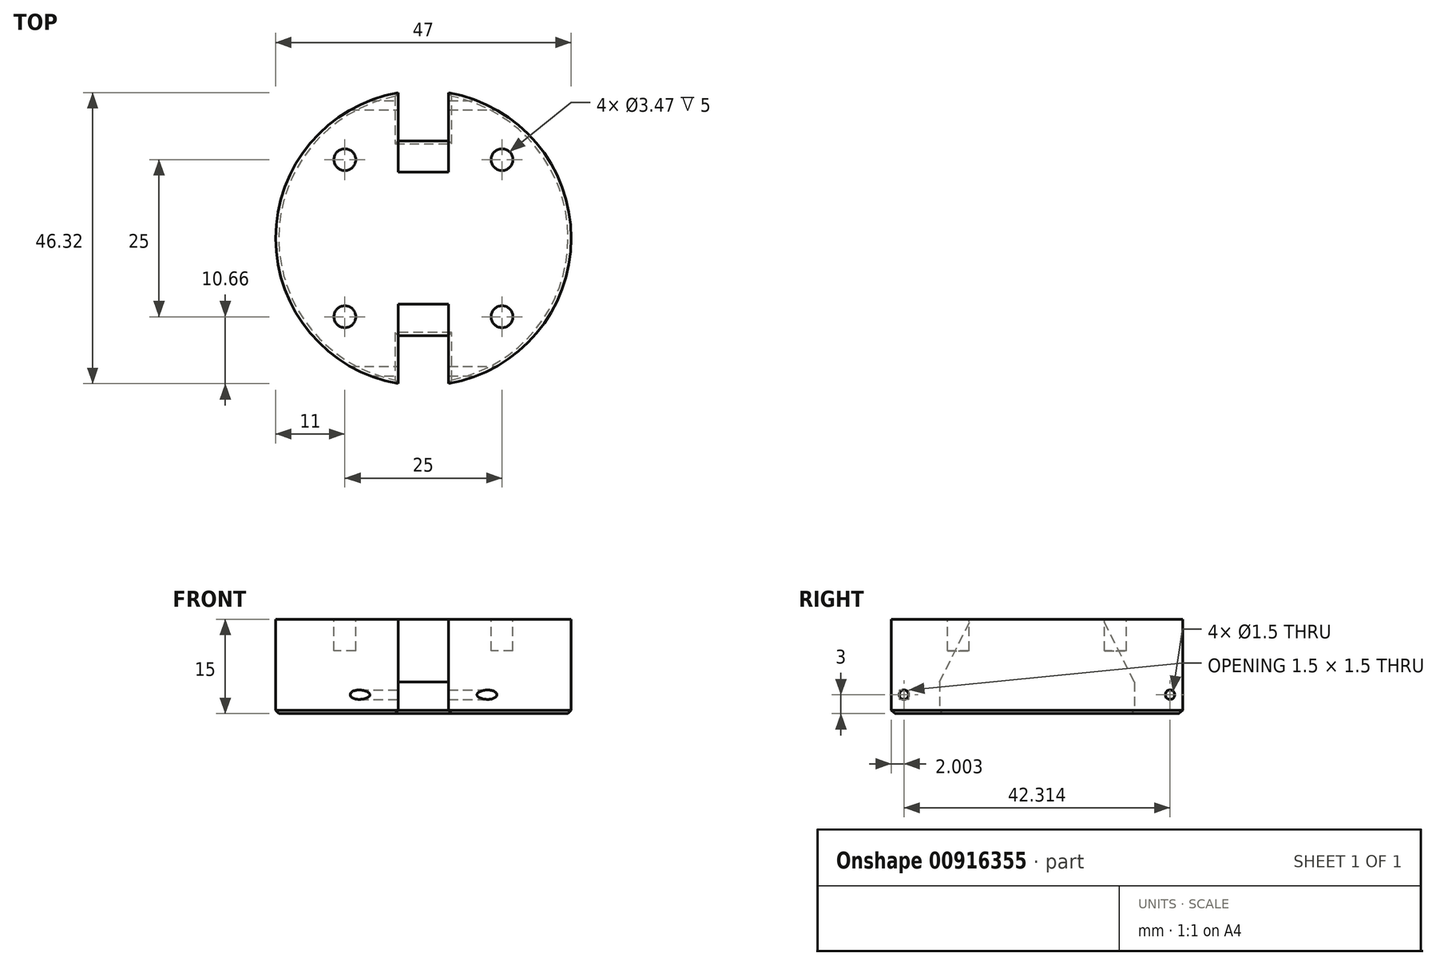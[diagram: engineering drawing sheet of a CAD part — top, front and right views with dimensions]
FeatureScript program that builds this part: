
annotation { "Feature Type Name" : "Feature", "Feature Type Description" : "" }
export const myFeature = defineFeature(function(context is Context, id is Id, definition is map)
    precondition{}
    {
        {
            var Q0;
            Q0=qCreatedBy(makeId("Top.planeOp"),FACE);
            var sketch = newSketch(context, id + "F0", { "sketchPlane" : qUnion([Q0])});
            skCircle(sketch, "E0", {"center": v(0, 0) * mm, "radius": 23.5 * mm});
            skSolve(sketch);
        }
        {
            var Q0;
            Q0=makeQuery(id+"F0.imprint","IMPRINT",FACE,{"disambiguationData":[TD([[makeQuery(id+"F0.imprint","IMPRINT",EDGE,{"derivedFrom":sQuery(id+"F0.wireOp",EDGE,"E0")}),1.0]])]});
            extrude(context, id + "F1", {"entities" : qUnion([Q0]), "depth" : 15 * mm, "offsetDistance" : 25 * mm});
        }
        {
            var Q0;
            Q0=makeQuery(id+"F1.opExtrude","CAP_FACE",FACE,{"disambiguationData":[OSD([sQuery(id+"F0.wireOp",EDGE,"E0")])],"isStart":true});
            var sketch = newSketch(context, id + "F2", { "sketchPlane" : qUnion([Q0])});
            skLineSegment(sketch, "E1.bottom", {"start": v(0, 23.5) * mm, "end": v(4, 23.5) * mm});
            skLineSegment(sketch, "E1.top", {"start": v(0, 15.5) * mm, "end": v(4, 15.5) * mm});
            skLineSegment(sketch, "E1.left", {"start": v(0, 23.5) * mm, "end": v(0, 15.5) * mm});
            skLineSegment(sketch, "E1.right", {"start": v(4, 23.5) * mm, "end": v(4, 15.5) * mm});
            skLineSegment(sketch, "E2.MirrorCS", {"start": v(0, 23.5) * mm, "end": v(-4, 23.5) * mm});
            skLineSegment(sketch, "E3.MirrorCS", {"start": v(0, 15.5) * mm, "end": v(-4, 15.5) * mm});
            skLineSegment(sketch, "E4.MirrorCS", {"start": v(-4, 23.5) * mm, "end": v(-4, 15.5) * mm});
            skLineSegment(sketch, "E5.MirrorCS", {"start": v(0, -23.5) * mm, "end": v(0, -15.5) * mm});
            skLineSegment(sketch, "E6.MirrorCS", {"start": v(0, -15.5) * mm, "end": v(-4, -15.5) * mm});
            skLineSegment(sketch, "E7.MirrorCS", {"start": v(4, -23.5) * mm, "end": v(4, -15.5) * mm});
            skLineSegment(sketch, "E8.MirrorCS", {"start": v(0, -15.5) * mm, "end": v(4, -15.5) * mm});
            skLineSegment(sketch, "E9.MirrorCS", {"start": v(0, -23.5) * mm, "end": v(-4, -23.5) * mm});
            skLineSegment(sketch, "E10.MirrorCS", {"start": v(0, -23.5) * mm, "end": v(4, -23.5) * mm});
            skLineSegment(sketch, "E11.MirrorCS", {"start": v(-4, -23.5) * mm, "end": v(-4, -15.5) * mm});
            skSolve(sketch);
        }
        {
            var Q0;
            {var subQ0=sQuery(id+"F2.wireOp",EDGE,"E9.MirrorCS");Q0=makeQuery(id+"F2.imprint","IMPRINT",FACE,{"disambiguationData":[TD([[makeQuery(id+"F2.imprint","IMPRINT",EDGE,{"derivedFrom":subQ0}),-1.0]])]});}
            var Q1;
            {var subQ0=sQuery(id+"F2.wireOp",EDGE,"E10.MirrorCS");Q1=makeQuery(id+"F2.imprint","IMPRINT",FACE,{"disambiguationData":[TD([[makeQuery(id+"F2.imprint","IMPRINT",EDGE,{"derivedFrom":subQ0}),1.0]])]});}
            var Q2;
            {var subQ0=sQuery(id+"F2.wireOp",EDGE,"E6.MirrorCS");Q2=makeQuery(id+"F2.imprint","IMPRINT",FACE,{"disambiguationData":[TD([[makeQuery(id+"F2.imprint","IMPRINT",EDGE,{"derivedFrom":subQ0}),1.0]])]});}
            var Q3;
            {var subQ4=sQuery(id+"F2.wireOp",EDGE,"E5.MirrorCS");Q3=makeQuery(id+"F2.imprint","IMPRINT",FACE,{"disambiguationData":[TD([[makeQuery(id+"F2.imprint","IMPRINT",EDGE,{"derivedFrom":subQ4}),-1.0]])]});}
            var Q4;
            {var subQ0=sQuery(id+"F2.wireOp",EDGE,"E1.top");Q4=makeQuery(id+"F2.imprint","IMPRINT",FACE,{"disambiguationData":[TD([[makeQuery(id+"F2.imprint","IMPRINT",EDGE,{"derivedFrom":subQ0}),1.0]])]});}
            var Q5;
            {var subQ0=sQuery(id+"F2.wireOp",EDGE,"E1.left");Q5=makeQuery(id+"F2.imprint","IMPRINT",FACE,{"disambiguationData":[TD([[makeQuery(id+"F2.imprint","IMPRINT",EDGE,{"derivedFrom":subQ0}),-1.0]])]});}
            var Q6;
            {var subQ0=sQuery(id+"F2.wireOp",EDGE,"E1.bottom");Q6=makeQuery(id+"F2.imprint","IMPRINT",FACE,{"disambiguationData":[TD([[makeQuery(id+"F2.imprint","IMPRINT",EDGE,{"derivedFrom":subQ0}),-1.0]])]});}
            var Q7;
            {var subQ0=sQuery(id+"F2.wireOp",EDGE,"E2.MirrorCS");Q7=makeQuery(id+"F2.imprint","IMPRINT",FACE,{"disambiguationData":[TD([[makeQuery(id+"F2.imprint","IMPRINT",EDGE,{"derivedFrom":subQ0}),1.0]])]});}
            extrude(context, id + "F3", {"entities" : qUnion([Q0, Q1, Q2, Q3, Q4, Q5, Q6, Q7]), "operationType" : NewBodyOperationType.REMOVE, "oppositeDirection" : true, "depth" : 25 * mm, "offsetDistance" : 25 * mm});
        }
        {
            var Q0;
            Q0=makeQuery(id+"F3.boolean.opBoolean","INTERSECT",EDGE,{"derivedFrom":[makeQuery(id+"F1.opExtrude","CAP_FACE",FACE,{"disambiguationData":[OSD([sQuery(id+"F0.wireOp",EDGE,"E0")])],"isStart":false}),makeQuery(id+"F3.opExtrude","SWEPT_FACE",FACE,{"disambiguationData":[OSD([sQuery(id+"F2.wireOp",EDGE,"E1.top"),sQuery(id+"F2.wireOp",EDGE,"E3.MirrorCS")])]})]});
            chamfer(context, id + "F4", {"entities" : qUnion([Q0]), "chamferType" : ChamferType.TWO_OFFSETS, "width1" : 10 * mm, "oppositeDirection" : false, "width2" : 5 * mm, "tangentPropagation" : true});
        }
        {
            var Q0;
            Q0=makeQuery(id+"F3.boolean.opBoolean","INTERSECT",EDGE,{"derivedFrom":[makeQuery(id+"F1.opExtrude","CAP_FACE",FACE,{"disambiguationData":[OSD([sQuery(id+"F0.wireOp",EDGE,"E0")])],"isStart":false}),makeQuery(id+"F3.opExtrude","SWEPT_FACE",FACE,{"disambiguationData":[OSD([sQuery(id+"F2.wireOp",EDGE,"E6.MirrorCS"),sQuery(id+"F2.wireOp",EDGE,"E8.MirrorCS")])]})]});
            chamfer(context, id + "F5", {"entities" : qUnion([Q0]), "chamferType" : ChamferType.TWO_OFFSETS, "width1" : 10 * mm, "oppositeDirection" : false, "width2" : 5 * mm, "tangentPropagation" : true});
        }
        {
            var Q0;
            Q0=qCreatedBy(makeId("Right.planeOp"),FACE);
            var sketch = newSketch(context, id + "F6", { "sketchPlane" : qUnion([Q0])});
            skLineSegment(sketch, "E12.bottom", {"start": v(-23.16, 0) * mm, "end": v(-21.16, 0) * mm});
            skLineSegment(sketch, "E12.top", {"start": v(-23.16, 3) * mm, "end": v(-21.16, 3) * mm});
            skLineSegment(sketch, "E12.left", {"start": v(-23.16, 0) * mm, "end": v(-23.16, 3) * mm});
            skLineSegment(sketch, "E12.right", {"start": v(-21.16, 0) * mm, "end": v(-21.16, 3) * mm});
            skCircle(sketch, "E13", {"center": v(-21.16, 3) * mm, "radius": 0.75 * mm});
            skSolve(sketch);
        }
        {
            var Q0;
            Q0=qCreatedBy(makeId("Right.planeOp"),FACE);
            var sketch = newSketch(context, id + "F7", { "sketchPlane" : qUnion([Q0])});
            skCircle(sketch, "E14", {"center": v(-21.16, 3) * mm, "radius": 0.75 * mm});
            skCircle(sketch, "E15.MirrorC", {"center": v(21.16, 3) * mm, "radius": 0.75 * mm});
            skSolve(sketch);
        }
        {
            var Q0;
            Q0 = qSketchRegion(id + "F7", true);
            extrude(context, id + "F8", {"entities" : qUnion([Q0]), "operationType" : NewBodyOperationType.REMOVE, "endBound" : BoundingType.SYMMETRIC, "oppositeDirection" : true, "depth" : 25 * mm, "offsetDistance" : 25 * mm});
        }
        {
            var Q0;
            Q0=makeQuery(id+"F1.opExtrude","CAP_FACE",FACE,{"disambiguationData":[OSD([sQuery(id+"F0.wireOp",EDGE,"E0")])],"isStart":false});
            var sketch = newSketch(context, id + "F9", { "sketchPlane" : qUnion([Q0])});
            skLineSegment(sketch, "E16.bottom", {"start": v(12.5, 12.5) * mm, "end": v(-12.5, 12.5) * mm});
            skLineSegment(sketch, "E16.top", {"start": v(12.5, -12.5) * mm, "end": v(-12.5, -12.5) * mm});
            skLineSegment(sketch, "E16.left", {"start": v(12.5, 12.5) * mm, "end": v(12.5, -12.5) * mm});
            skLineSegment(sketch, "E16.right", {"start": v(-12.5, 12.5) * mm, "end": v(-12.5, -12.5) * mm});
            skPoint(sketch, "E16.middle", {"position": v(0, 0) * mm});
            skSolve(sketch);
        }
        {
            var Q0;
            {var subQ7=sQuery(id+"F9.wireOp",EDGE,"E16.left");Q0=makeQuery(id+"F9.imprint","IMPRINT",FACE,{"disambiguationData":[TD([[makeQuery(id+"F9.imprint","IMPRINT",EDGE,{"derivedFrom":subQ7}),-1.0]])]});}
            var sketch = newSketch(context, id + "F10", { "sketchPlane" : qUnion([Q0])});
            skCircle(sketch, "E17", {"center": v(-12.5, 12.5) * mm, "radius": 1.74 * mm});
            skCircle(sketch, "E18", {"center": v(12.5, -12.5) * mm, "radius": 1.74 * mm});
            skCircle(sketch, "E19", {"center": v(12.5, 12.5) * mm, "radius": 1.74 * mm});
            skCircle(sketch, "E20", {"center": v(-12.5, -12.5) * mm, "radius": 1.74 * mm});
            skSolve(sketch);
        }
        {
            var Q0;
            {var subQ0=sQuery(id+"F10.wireOp",EDGE,"E17");var subQ1=sQuery(id+"F9.wireOp",EDGE,"E16.right");var subQ5=makeQuery(id+"F9.imprint","IMPRINT",EDGE,{"derivedFrom":subQ1});var subQ6=makeQuery(id+"F10.imprint","INTERSECT",VERTEX,{"derivedFrom":[subQ5,subQ0]});Q0=makeQuery(id+"F10.imprint","IMPRINT",FACE,{"disambiguationData":[TD([[makeQuery(id+"F10.imprint","IMPRINT",EDGE,{"disambiguationData":[TD([[subQ6,1.0]])],"derivedFrom":subQ0}),1.0]])]});}
            var Q1;
            {var subQ0=sQuery(id+"F10.wireOp",EDGE,"E17");var subQ1=sQuery(id+"F9.wireOp",EDGE,"E16.right");var subQ5=makeQuery(id+"F9.imprint","IMPRINT",EDGE,{"derivedFrom":subQ1});var subQ6=makeQuery(id+"F10.imprint","INTERSECT",VERTEX,{"derivedFrom":[subQ5,subQ0]});Q1=makeQuery(id+"F10.imprint","IMPRINT",FACE,{"disambiguationData":[TD([[makeQuery(id+"F10.imprint","IMPRINT",EDGE,{"disambiguationData":[TD([[subQ6,-1.0]])],"derivedFrom":subQ0}),1.0]])]});}
            var Q2;
            {var subQ0=sQuery(id+"F10.wireOp",EDGE,"E20");var subQ1=sQuery(id+"F9.wireOp",EDGE,"E16.right");var subQ5=makeQuery(id+"F9.imprint","IMPRINT",EDGE,{"derivedFrom":subQ1});var subQ6=makeQuery(id+"F10.imprint","INTERSECT",VERTEX,{"derivedFrom":[subQ5,subQ0]});Q2=makeQuery(id+"F10.imprint","IMPRINT",FACE,{"disambiguationData":[TD([[makeQuery(id+"F10.imprint","IMPRINT",EDGE,{"disambiguationData":[TD([[subQ6,-1.0]])],"derivedFrom":subQ0}),1.0]])]});}
            var Q3;
            {var subQ0=sQuery(id+"F10.wireOp",EDGE,"E20");var subQ1=sQuery(id+"F9.wireOp",EDGE,"E16.right");var subQ5=makeQuery(id+"F9.imprint","IMPRINT",EDGE,{"derivedFrom":subQ1});var subQ6=makeQuery(id+"F10.imprint","INTERSECT",VERTEX,{"derivedFrom":[subQ5,subQ0]});Q3=makeQuery(id+"F10.imprint","IMPRINT",FACE,{"disambiguationData":[TD([[makeQuery(id+"F10.imprint","IMPRINT",EDGE,{"disambiguationData":[TD([[subQ6,1.0]])],"derivedFrom":subQ0}),1.0]])]});}
            var Q4;
            {var subQ0=sQuery(id+"F10.wireOp",EDGE,"E18");var subQ1=sQuery(id+"F9.wireOp",EDGE,"E16.left");var subQ5=makeQuery(id+"F9.imprint","IMPRINT",EDGE,{"derivedFrom":subQ1});var subQ6=makeQuery(id+"F10.imprint","INTERSECT",VERTEX,{"derivedFrom":[subQ5,subQ0]});Q4=makeQuery(id+"F10.imprint","IMPRINT",FACE,{"disambiguationData":[TD([[makeQuery(id+"F10.imprint","IMPRINT",EDGE,{"disambiguationData":[TD([[subQ6,1.0]])],"derivedFrom":subQ0}),1.0]])]});}
            var Q5;
            {var subQ0=sQuery(id+"F10.wireOp",EDGE,"E19");var subQ1=sQuery(id+"F9.wireOp",EDGE,"E16.left");var subQ5=makeQuery(id+"F9.imprint","IMPRINT",EDGE,{"derivedFrom":subQ1});var subQ6=makeQuery(id+"F10.imprint","INTERSECT",VERTEX,{"derivedFrom":[subQ5,subQ0]});Q5=makeQuery(id+"F10.imprint","IMPRINT",FACE,{"disambiguationData":[TD([[makeQuery(id+"F10.imprint","IMPRINT",EDGE,{"disambiguationData":[TD([[subQ6,-1.0]])],"derivedFrom":subQ0}),1.0]])]});}
            var Q6;
            {var subQ0=sQuery(id+"F10.wireOp",EDGE,"E19");var subQ1=sQuery(id+"F9.wireOp",EDGE,"E16.left");var subQ5=makeQuery(id+"F9.imprint","IMPRINT",EDGE,{"derivedFrom":subQ1});var subQ6=makeQuery(id+"F10.imprint","INTERSECT",VERTEX,{"derivedFrom":[subQ5,subQ0]});Q6=makeQuery(id+"F10.imprint","IMPRINT",FACE,{"disambiguationData":[TD([[makeQuery(id+"F10.imprint","IMPRINT",EDGE,{"disambiguationData":[TD([[subQ6,1.0]])],"derivedFrom":subQ0}),1.0]])]});}
            var Q7;
            {var subQ0=sQuery(id+"F10.wireOp",EDGE,"E18");var subQ1=sQuery(id+"F9.wireOp",EDGE,"E16.left");var subQ5=makeQuery(id+"F9.imprint","IMPRINT",EDGE,{"derivedFrom":subQ1});var subQ6=makeQuery(id+"F10.imprint","INTERSECT",VERTEX,{"derivedFrom":[subQ5,subQ0]});Q7=makeQuery(id+"F10.imprint","IMPRINT",FACE,{"disambiguationData":[TD([[makeQuery(id+"F10.imprint","IMPRINT",EDGE,{"disambiguationData":[TD([[subQ6,-1.0]])],"derivedFrom":subQ0}),1.0]])]});}
            extrude(context, id + "F11", {"entities" : qUnion([Q0, Q1, Q2, Q3, Q4, Q5, Q6, Q7]), "operationType" : NewBodyOperationType.REMOVE, "oppositeDirection" : true, "depth" : 5 * mm, "offsetDistance" : 25 * mm});
        }
        {
            var Q0;
            Q0=makeQuery(id+"F1.opExtrude","CAP_FACE",FACE,{"disambiguationData":[OSD([sQuery(id+"F0.wireOp",EDGE,"E0")])],"isStart":true});
            chamfer(context, id + "F12", {"entities" : qUnion([Q0]), "width" : .5 * mm, "tangentPropagation" : true});
        }
    });
